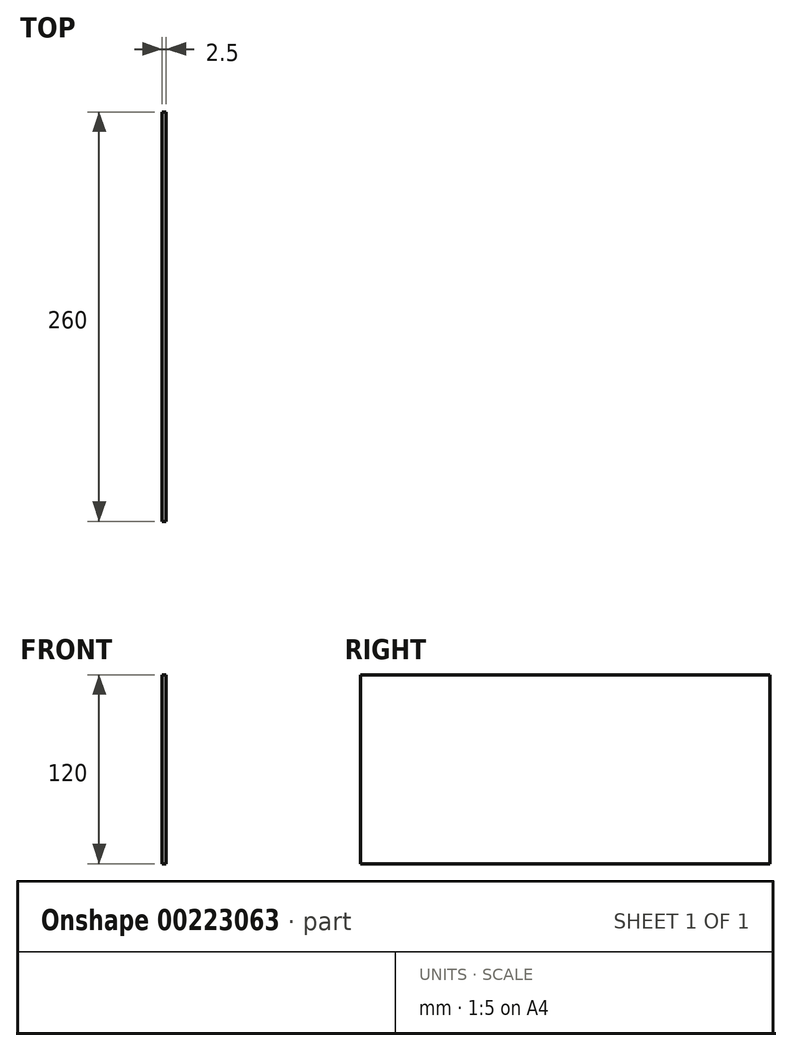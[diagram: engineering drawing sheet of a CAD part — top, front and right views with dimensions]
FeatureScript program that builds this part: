
annotation { "Feature Type Name" : "Feature", "Feature Type Description" : "" }
export const myFeature = defineFeature(function(context is Context, id is Id, definition is map)
    precondition{}
    {
        {
            var Q0;
            Q0=qCreatedBy(makeId("Right.planeOp"),FACE);
            var sketch = newSketch(context, id + "F0", { "sketchPlane" : qUnion([Q0])});
            skLineSegment(sketch, "E0.bottom", {"start": v(130, -60) * mm, "end": v(-130, -60) * mm});
            skLineSegment(sketch, "E0.top", {"start": v(130, 60) * mm, "end": v(-130, 60) * mm});
            skLineSegment(sketch, "E0.left", {"start": v(130, -60) * mm, "end": v(130, 60) * mm});
            skLineSegment(sketch, "E0.right", {"start": v(-130, -60) * mm, "end": v(-130, 60) * mm});
            skPoint(sketch, "E0.middle", {"position": v(0, 0) * mm});
            skSolve(sketch);
        }
        {
            var Q0;
            Q0=makeQuery(id+"F0.imprint","IMPRINT",FACE,{"disambiguationData":[TD([[makeQuery(id+"F0.imprint","IMPRINT",EDGE,{"derivedFrom":sQuery(id+"F0.wireOp",EDGE,"E0.bottom")}),-1.0]])]});
            extrude(context, id + "F1", {"entities" : qUnion([Q0]), "depth" : 2.5 * mm});
        }
    });
